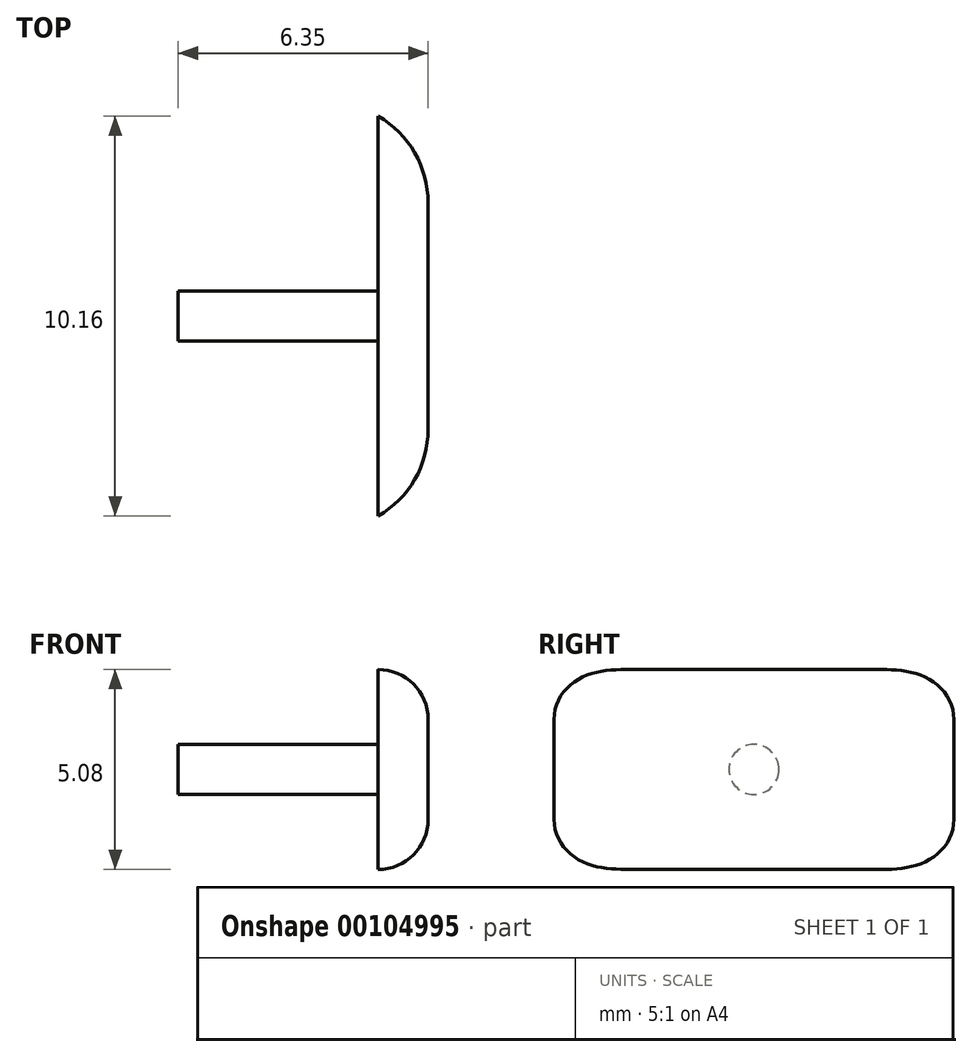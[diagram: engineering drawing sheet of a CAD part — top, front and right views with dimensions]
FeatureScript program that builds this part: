
annotation { "Feature Type Name" : "Feature", "Feature Type Description" : "" }
export const myFeature = defineFeature(function(context is Context, id is Id, definition is map)
    precondition{}
    {
        {
            var Q0;
            Q0=qCreatedBy(makeId("Top.planeOp"),FACE);
            var sketch = newSketch(context, id + "F0", { "sketchPlane" : qUnion([Q0])});
            skLineSegment(sketch, "E0.bottom", {"start": v(0, 7.85) * mm, "end": v(1.27, 7.85) * mm});
            skLineSegment(sketch, "E0.top", {"start": v(0, -2.31) * mm, "end": v(1.27, -2.31) * mm});
            skLineSegment(sketch, "E0.left", {"start": v(0, 7.85) * mm, "end": v(0, -2.31) * mm});
            skLineSegment(sketch, "E0.right", {"start": v(1.27, 7.85) * mm, "end": v(1.27, -2.31) * mm});
            skSolve(sketch);
        }
        {
            var Q0;
            Q0=makeQuery(id+"F0.imprint","IMPRINT",FACE,{"disambiguationData":[TD([[makeQuery(id+"F0.imprint","IMPRINT",EDGE,{"derivedFrom":sQuery(id+"F0.wireOp",EDGE,"E0.bottom")}),-1.0]])]});
            extrude(context, id + "F1", {"entities" : qUnion([Q0]), "depth" : 5.08 * mm});
        }
        {
            var Q0;
            Q0=makeQuery(id+"F1.opExtrude","SWEPT_EDGE",EDGE,{"disambiguationData":[OSD([sQuery(id+"F0.wireOp",EDGE,"E0.bottom"),sQuery(id+"F0.wireOp",EDGE,"E0.right")])]});
            var Q1;
            Q1=makeQuery(id+"F1.opExtrude","SWEPT_EDGE",EDGE,{"disambiguationData":[OSD([sQuery(id+"F0.wireOp",EDGE,"E0.top"),sQuery(id+"F0.wireOp",EDGE,"E0.right")])]});
            fillet(context, id + "F2", {"entities" : qUnion([Q0, Q1]), "radius" : 2.54 * mm, "tangentPropagation" : true, "allowEdgeOverflow" : false});
        }
        {
            var Q0;
            {var subQ0=sQuery(id+"F0.wireOp",EDGE,"E0.right");var subQ1=sQuery(id+"F0.wireOp",EDGE,"E0.bottom");Q0=makeQuery(id+"F2.opFillet","BLEND_EDGE",EDGE,{"blendedFrom":[makeQuery(id+"F1.opExtrude","SWEPT_EDGE",EDGE,{"disambiguationData":[OSD([subQ1,subQ0])]}),makeQuery(id+"F1.opExtrude","CAP_FACE",FACE,{"disambiguationData":[OSD([subQ1,sQuery(id+"F0.wireOp",EDGE,"E0.top"),sQuery(id+"F0.wireOp",EDGE,"E0.left"),subQ0])],"isStart":false})],"blendedInto":[makeQuery(id+"F1.opExtrude","CAP_FACE",FACE,{"disambiguationData":[OSD([subQ1,sQuery(id+"F0.wireOp",EDGE,"E0.top"),sQuery(id+"F0.wireOp",EDGE,"E0.left"),subQ0])],"isStart":false})]});}
            var Q1;
            Q1=makeQuery(id+"F1.opExtrude","CAP_EDGE",EDGE,{"disambiguationData":[OSD([sQuery(id+"F0.wireOp",EDGE,"E0.right")])],"isStart":false});
            var Q2;
            {var subQ0=sQuery(id+"F0.wireOp",EDGE,"E0.right");var subQ1=sQuery(id+"F0.wireOp",EDGE,"E0.top");Q2=makeQuery(id+"F2.opFillet","BLEND_EDGE",EDGE,{"blendedFrom":[makeQuery(id+"F1.opExtrude","SWEPT_EDGE",EDGE,{"disambiguationData":[OSD([subQ1,subQ0])]}),makeQuery(id+"F1.opExtrude","CAP_FACE",FACE,{"disambiguationData":[OSD([sQuery(id+"F0.wireOp",EDGE,"E0.bottom"),subQ1,sQuery(id+"F0.wireOp",EDGE,"E0.left"),subQ0])],"isStart":false})],"blendedInto":[makeQuery(id+"F1.opExtrude","CAP_FACE",FACE,{"disambiguationData":[OSD([sQuery(id+"F0.wireOp",EDGE,"E0.bottom"),subQ1,sQuery(id+"F0.wireOp",EDGE,"E0.left"),subQ0])],"isStart":false})]});}
            var Q3;
            {var subQ0=sQuery(id+"F0.wireOp",EDGE,"E0.right");var subQ1=sQuery(id+"F0.wireOp",EDGE,"E0.bottom");Q3=makeQuery(id+"F2.opFillet","BLEND_EDGE",EDGE,{"blendedFrom":[makeQuery(id+"F1.opExtrude","SWEPT_EDGE",EDGE,{"disambiguationData":[OSD([subQ1,subQ0])]}),makeQuery(id+"F1.opExtrude","CAP_FACE",FACE,{"disambiguationData":[OSD([subQ1,sQuery(id+"F0.wireOp",EDGE,"E0.top"),sQuery(id+"F0.wireOp",EDGE,"E0.left"),subQ0])],"isStart":true})],"blendedInto":[makeQuery(id+"F1.opExtrude","CAP_FACE",FACE,{"disambiguationData":[OSD([subQ1,sQuery(id+"F0.wireOp",EDGE,"E0.top"),sQuery(id+"F0.wireOp",EDGE,"E0.left"),subQ0])],"isStart":true})]});}
            fillet(context, id + "F3", {"entities" : qUnion([Q0, Q1, Q2, Q3]), "radius" : 1.27 * mm, "tangentPropagation" : true, "allowEdgeOverflow" : false});
        }
        {
            var Q0;
            Q0=makeQuery(id+"F1.opExtrude","SWEPT_FACE",FACE,{"disambiguationData":[OSD([sQuery(id+"F0.wireOp",EDGE,"E0.left")])]});
            var sketch = newSketch(context, id + "F4", { "sketchPlane" : qUnion([Q0])});
            skCircle(sketch, "E1", {"center": v(-2.77, 2.54) * mm, "radius": 0.64 * mm});
            skPoint(sketch, "E1.centerSnap0", {"position": v(-2.77, 0) * mm});
            skPoint(sketch, "E1.centerSnap1", {"position": v(-7.85, 2.54) * mm});
            skSolve(sketch);
        }
        {
            var Q0;
            Q0=makeQuery(id+"F4.imprint","IMPRINT",FACE,{"disambiguationData":[TD([[makeQuery(id+"F4.imprint","IMPRINT",EDGE,{"derivedFrom":sQuery(id+"F4.wireOp",EDGE,"E1")}),1.0]])]});
            extrude(context, id + "F5", {"entities" : qUnion([Q0]), "operationType" : NewBodyOperationType.ADD, "depth" : 5.08 * mm});
        }
    });
